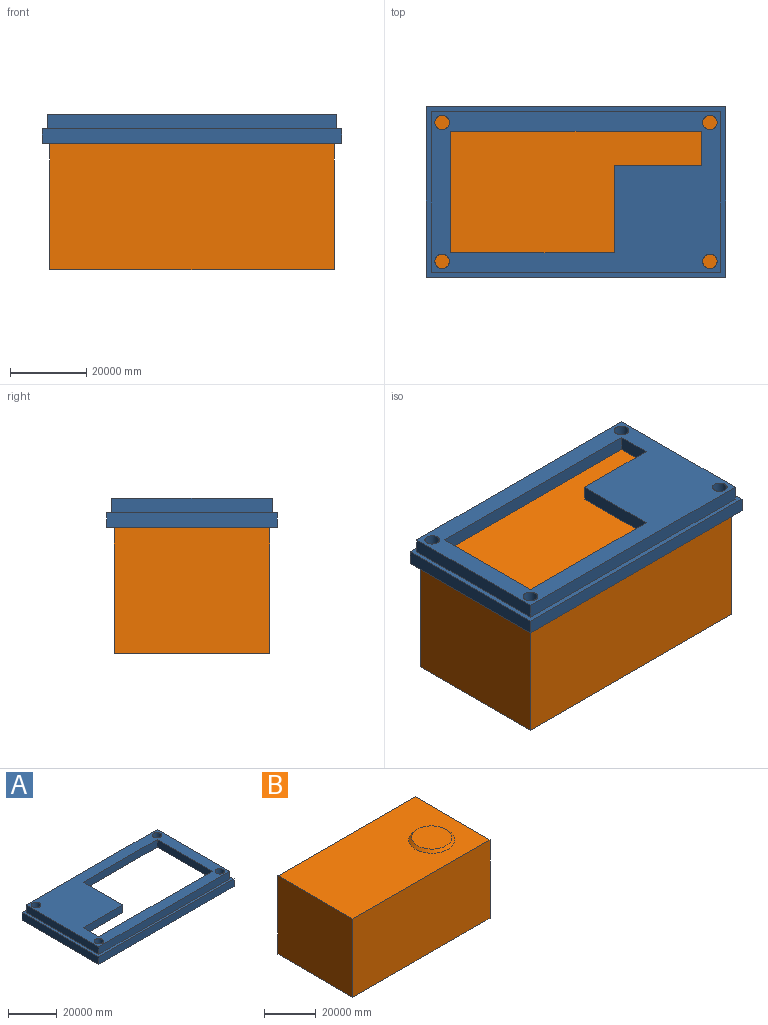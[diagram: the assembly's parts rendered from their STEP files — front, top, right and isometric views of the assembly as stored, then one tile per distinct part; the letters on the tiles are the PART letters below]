
ASSEMBLY  parts=2 mates=1
PART A: 28 faces, bbox 78536.8x44678.6x7620 mm
  f0: plane 17780x17780mm, normal (0,0,-1), area 248286664.8mm2, adj f1
  f1: cylinder r=8890mm len=17780mm, axis (0,0,-1), area 106408570.6mm2, adj f0,f12
  f2: plane 31978.6x3810mm, normal (-1,0,0), area 121838466mm2, adj f3,f7,f12,f13
  f3: plane 65836.8x3810mm, normal (0,1,0), area 250838208mm2, adj f2,f4,f12,f13
  f4: plane 9118.6x3810mm, normal (1,0,0), area 34741866mm2, adj f3,f5,f12,f13
  f5: plane 22860x3810mm, normal (0,-1,0), area 87096600mm2, adj f4,f6,f12,f13
  f6: plane 22860x3810mm, normal (1,0,0), area 87096600mm2, adj f5,f7,f12,f13
  f7: plane 42976.8x3810mm, normal (0,-1,0), area 163741608mm2, adj f2,f6,f12,f13
  f8: cylinder r=1905mm len=3810mm, axis (0,0,-1), area 45603673.1mm2, adj f12,f13
  f9: cylinder r=1905mm len=3810mm, axis (0,0,-1), area 45603673.1mm2, adj f12,f13
  f10: cylinder r=1905mm len=3810mm, axis (0,0,-1), area 45603673.1mm2, adj f12,f13
  f11: cylinder r=1905mm len=3810mm, axis (0,0,-1), area 45603673.1mm2, adj f12,f13
  f12: plane 74726.8x40868.6mm, normal (0,0,-1), area 1177300268.1mm2, adj f1,f2,f3,f4,f5,f6,f7,f8
  f13: plane 75996.8x42138.6mm, normal (0,0,1), area 1574005990.9mm2, adj f2,f3,f4,f5,f6,f7,f8,f9
  f14: plane 74726.8x3810mm, normal (0,1,0), area 284709108mm2, adj f12,f15,f17,f24
  f15: plane 40868.6x3810mm, normal (-1,0,0), area 155709366mm2, adj f12,f14,f16,f24
  f16: plane 74726.8x3810mm, normal (0,-1,0), area 284709108mm2, adj f12,f15,f17,f24
  f17: plane 40868.6x3810mm, normal (1,0,0), area 155709366mm2, adj f12,f14,f16,f24
  f18: plane 78536.8x3810mm, normal (0,1,0), area 299225208mm2, adj f23,f24,f25,f26
  f19: plane 75996.8x3810mm, normal (0,-1,0), area 289547808mm2, adj f13,f20,f22,f26
  f20: plane 42138.6x3810mm, normal (-1,0,0), area 160548066mm2, adj f13,f19,f21,f26
  f21: plane 75996.8x3810mm, normal (0,1,0), area 289547808mm2, adj f13,f20,f22,f26
  f22: plane 42138.6x3810mm, normal (1,0,0), area 160548066mm2, adj f13,f19,f21,f26
  f23: plane 44678.6x3810mm, normal (-1,0,0), area 170225466mm2, adj f18,f24,f26,f27
  f24: plane 78536.8x44678.6mm, normal (0,0,-1), area 454934574mm2, adj f14,f15,f16,f17,f18,f23,f25,f27
  f25: plane 44678.6x3810mm, normal (1,0,0), area 170225466mm2, adj f18,f24,f26,f27
  f26: plane 78536.8x44678.6mm, normal (0,0,1), area 306515516mm2, adj f18,f19,f20,f21,f22,f23,f25,f27
  f27: plane 78536.8x3810mm, normal (0,-1,0), area 299225208mm2, adj f23,f24,f25,f26
PART B: 8 faces, bbox 74726.8x40868.6x38125.4 mm
  f0: plane 15494x15494mm, normal (0,0,1), area 188545853mm2, adj f1
  f1: cone r=0mm half-angle=45deg, axis (0,0,-1), area 84486266.2mm2, adj f0,f5
  f2: plane 74726.8x36982.4mm, normal (0,-1,0), area 2763576408.3mm2, adj f3,f4,f5,f6
  f3: plane 74726.8x40868.6mm, normal (0,0,-1), area 3053979698.5mm2, adj f2,f4,f6,f7
  f4: plane 40868.6x36982.4mm, normal (1,0,0), area 1511418912.6mm2, adj f2,f3,f5,f7
  f5: plane 74726.8x40868.6mm, normal (0,0,1), area 2805693033.7mm2, adj f1,f2,f4,f6,f7
  f6: plane 40868.6x36982.4mm, normal (-1,0,0), area 1511418912.6mm2, adj f2,f3,f5,f7
  f7: plane 74726.8x36982.4mm, normal (0,1,0), area 2763576408.3mm2, adj f3,f4,f5,f6
PLACE A rot(axis=(0,0,1),180deg) t=(42717.32,24142.47,13827.61)mm
PLACE B t=(-33914.48,22237.47,-19344.79)mm
MATE cylindrical A.f1 <-> B.f1  axis (0,0,-1) through (24937.32,-2756.13,17637.61)mm
